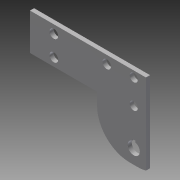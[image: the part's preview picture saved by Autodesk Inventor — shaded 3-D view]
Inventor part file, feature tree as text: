
AUTODESK INVENTOR PART (.ipt)
format: ipt  version: 2013 (Build 170138000, 138)  size: 179,200 bytes
history: native  units: in
note: dims shown in document units (in); Inventor stores cm internally (conversion verified against a paired STEP export)
features: sketch x6, other x6, reference x6, sheet_metal_op x1, extrude x1, fillet x1, plane x1
ambient origin geometry x8: Origin, YZ Plane, XZ Plane, XY Plane, X Axis, Y Axis, Z Axis, Center Point
feature tree (22):
  sheet_metal_op  "Face3"
  extrude  "Extrusion2"  Depth=0.25in
  sketch  "Sketch8"  dims[d8=0.125in]
  fillet  "Fillet1"  Radius=0.295in
  sketch  "Sketch11"  dims[d60=2.5in]
  plane  "Work Plane2"
  other  "Plate6"
  sketch  "Sketch7"  dims[d3=0.295in d4=0.25in d5=0.295in]
  reference  "Reference1"
  reference  "Reference2"
  sketch  "Sketch9"  dims[d19=0.25in]
  sketch  "Sketch10"  dims[d56=0.125in]
  reference  "Reference3"
  reference  "Reference4"
  sketch  "Sketch12"  dims[d61=0.4375in d62=0.375in d63=0.125in d67=0.125in d68=0.0in d69=2.053in d70=0.0in d71=1.125in d72=2.053in d75=0.125in d76=0.0in d77=0.125in d78=0.0in d79=0.125in d80=0.0in d81=1.0in d82=0.0469in d86=0.0938in d87=0.0469in d88=0.75in d89=0.125in d90=0.0in]
  reference  "Reference5"
  reference  "Reference6"
  other  "Cut1"
  other  "Cut3"
  other  "Cut4"
  other  "Cut5"
  other  "Cut6"
